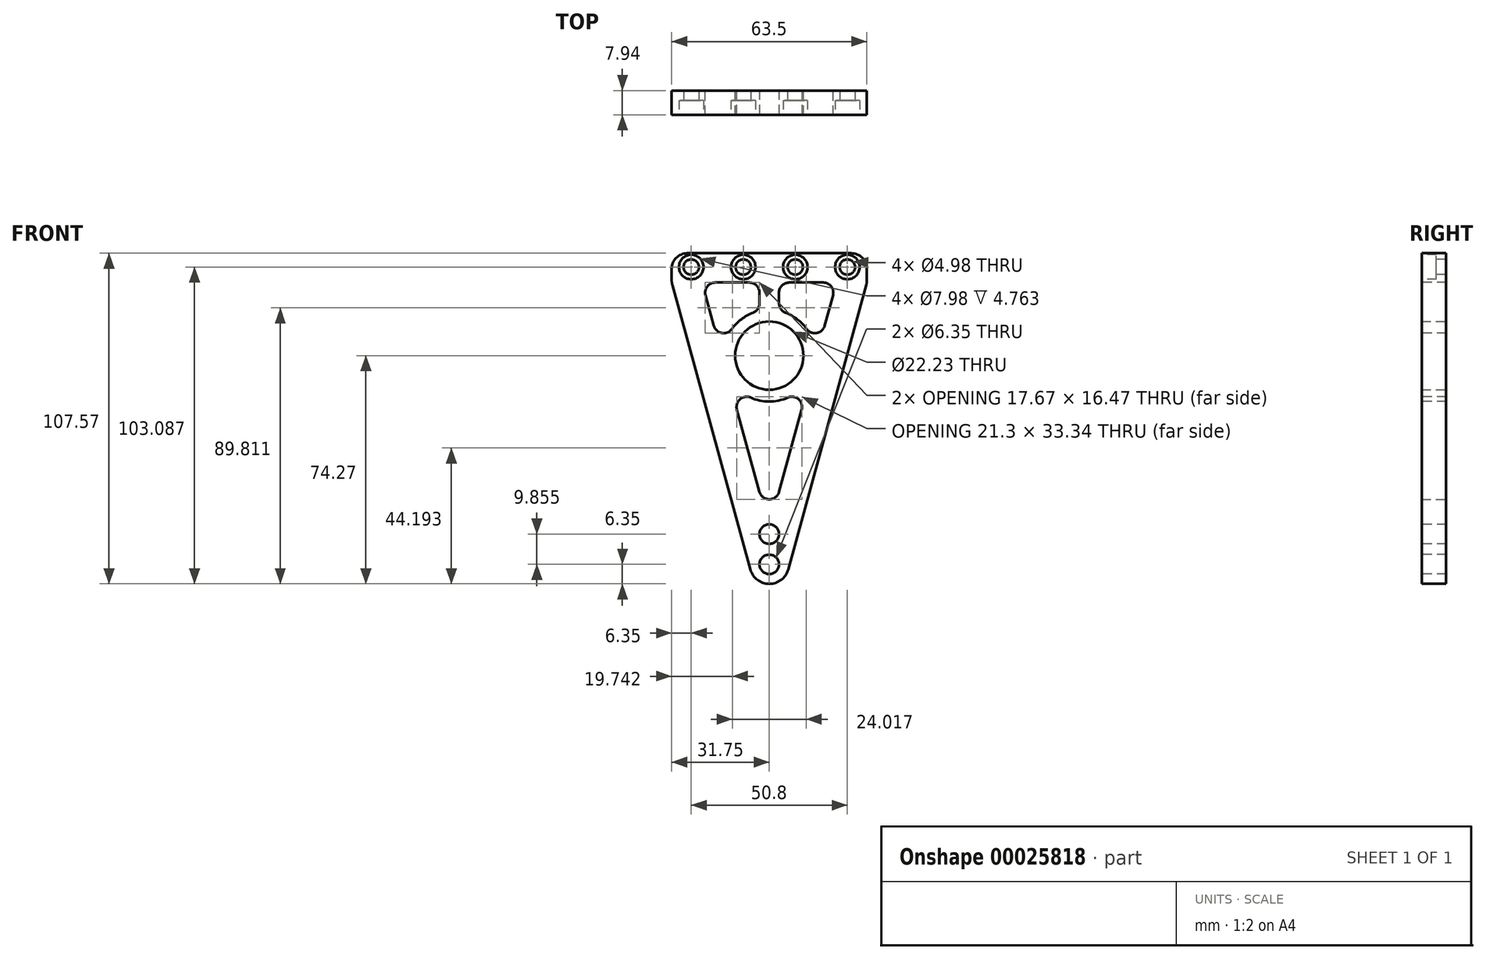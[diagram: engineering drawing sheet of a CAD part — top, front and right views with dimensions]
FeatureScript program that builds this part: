
annotation { "Feature Type Name" : "Feature", "Feature Type Description" : "" }
export const myFeature = defineFeature(function(context is Context, id is Id, definition is map)
    precondition{}
    {
        {
            var Q0;
            Q0=qCreatedBy(makeId("Front.planeOp"),FACE);
            var sketch = newSketch(context, id + "F0", { "sketchPlane" : qUnion([Q0])});
            skCircle(sketch, "E0", {"center": v(0, 0) * mm, "radius": 11.11 * mm});
            skLineSegment(sketch, "E1", {"start": v(0, 0) * mm, "end": v(0, 33.3) * mm, "construction": true});
            skLineSegment(sketch, "E2", {"start": v(0, 0) * mm, "end": v(25.23, 0) * mm, "construction": true});
            skLineSegment(sketch, "E3", {"start": v(-31.75, 33.3) * mm, "end": v(31.75, 33.3) * mm});
            skLineSegment(sketch, "E4", {"start": v(31.75, 33.3) * mm, "end": v(31.75, 23.77) * mm});
            skLineSegment(sketch, "E5", {"start": v(31.75, 23.77) * mm, "end": v(6.12, -69.6) * mm});
            skLineSegment(sketch, "E6", {"start": v(-6.12, -69.6) * mm, "end": v(-31.75, 23.77) * mm});
            skLineSegment(sketch, "E7", {"start": v(-31.75, 23.77) * mm, "end": v(-31.75, 33.3) * mm});
            skArc(sketch, "E8", {"start": v(-6.12, -69.6) * mm, "mid": v(0, -74.27) * mm, "end": v(6.12, -69.6) * mm});
            skSolve(sketch);
        }
        {
            var Q0;
            Q0=makeQuery(id+"F0.imprint","IMPRINT",FACE,{"disambiguationData":[TD([[makeQuery(id+"F0.imprint","IMPRINT",EDGE,{"derivedFrom":sQuery(id+"F0.wireOp",EDGE,"E0")}),-1.0]])]});
            extrude(context, id + "F1", {"entities" : qUnion([Q0]), "depth" : 6.35 * mm});
        }
        {
            var Q0;
            Q0=makeQuery(id+"F1.opExtrude","CAP_FACE",FACE,{"disambiguationData":[OSD([sQuery(id+"F0.wireOp",EDGE,"E0"),sQuery(id+"F0.wireOp",EDGE,"E3"),sQuery(id+"F0.wireOp",EDGE,"E4"),sQuery(id+"F0.wireOp",EDGE,"E5"),sQuery(id+"F0.wireOp",EDGE,"E6"),sQuery(id+"F0.wireOp",EDGE,"E7"),sQuery(id+"F0.wireOp",EDGE,"E8")])],"isStart":false});
            var sketch = newSketch(context, id + "F2", { "sketchPlane" : qUnion([Q0])});
            skLineSegment(sketch, "E9.0", {"start": v(21.87, 23.77) * mm, "end": v(3.17, 23.77) * mm});
            skLineSegment(sketch, "E9.2", {"start": v(0, -55.92) * mm, "end": v(13.77, -5.75) * mm});
            skLineSegment(sketch, "E9.3", {"start": v(-21.87, 23.77) * mm, "end": v(-14.78, -2.08) * mm});
            skArc(sketch, "E10", {"start": v(-13.77, -5.75) * mm, "mid": v(0, -14.92) * mm, "end": v(13.77, -5.75) * mm});
            skLineSegment(sketch, "E11.trimOffspring", {"start": v(-13.77, -5.75) * mm, "end": v(0, -55.92) * mm});
            skArc(sketch, "E12.trimOffspring", {"start": v(14.78, -2.08) * mm, "mid": v(12.25, 8.53) * mm, "end": v(3.18, 14.58) * mm});
            skLineSegment(sketch, "E13.trimOffspring", {"start": v(14.78, -2.08) * mm, "end": v(21.87, 23.77) * mm});
            skLineSegment(sketch, "E14", {"start": v(0, 0) * mm, "end": v(0, 33.3) * mm, "construction": true});
            skLineSegment(sketch, "E15.left", {"start": v(3.18, 14.58) * mm, "end": v(3.17, 23.77) * mm});
            skLineSegment(sketch, "E15.right", {"start": v(-3.18, 14.58) * mm, "end": v(-3.17, 23.77) * mm});
            skArc(sketch, "E16.trimOffspring", {"start": v(-3.18, 14.58) * mm, "mid": v(-12.25, 8.53) * mm, "end": v(-14.78, -2.08) * mm});
            skLineSegment(sketch, "E17.trimOffspring", {"start": v(-3.18, 23.77) * mm, "end": v(-21.87, 23.77) * mm});
            skSolve(sketch);
        }
        {
            var Q0;
            Q0=makeQuery(id+"F2.imprint","IMPRINT",FACE,{"disambiguationData":[TD([[makeQuery(id+"F2.imprint","IMPRINT",EDGE,{"derivedFrom":sQuery(id+"F2.wireOp",EDGE,"E9.0")}),1.0]])]});
            var Q1;
            Q1=makeQuery(id+"F2.imprint","IMPRINT",FACE,{"disambiguationData":[TD([[makeQuery(id+"F2.imprint","IMPRINT",EDGE,{"derivedFrom":sQuery(id+"F2.wireOp",EDGE,"E9.3")}),1.0]])]});
            var Q2;
            Q2=makeQuery(id+"F2.imprint","IMPRINT",FACE,{"disambiguationData":[TD([[makeQuery(id+"F2.imprint","IMPRINT",EDGE,{"derivedFrom":sQuery(id+"F2.wireOp",EDGE,"E9.2")}),1.0]])]});
            extrude(context, id + "F3", {"entities" : qUnion([Q0, Q1, Q2]), "operationType" : NewBodyOperationType.REMOVE, "endBound" : BoundingType.THROUGH_ALL, "oppositeDirection" : true, "depth" : 25.4 * mm});
        }
        {
            var Q0;
            Q0=makeQuery(id+"F3.boolean.opBoolean","COPY",EDGE,{"derivedFrom":makeQuery(id+"F3.opExtrude","SWEPT_EDGE",EDGE,{"disambiguationData":[OSD([sQuery(id+"F2.wireOp",EDGE,"E9.3"),sQuery(id+"F2.wireOp",EDGE,"E17.trimOffspring")])]})});
            var Q1;
            Q1=makeQuery(id+"F3.boolean.opBoolean","COPY",EDGE,{"derivedFrom":makeQuery(id+"F3.opExtrude","SWEPT_EDGE",EDGE,{"disambiguationData":[OSD([sQuery(id+"F2.wireOp",EDGE,"E15.right"),sQuery(id+"F2.wireOp",EDGE,"E16.trimOffspring")])]})});
            var Q2;
            Q2=makeQuery(id+"F3.boolean.opBoolean","COPY",EDGE,{"derivedFrom":makeQuery(id+"F3.opExtrude","SWEPT_EDGE",EDGE,{"disambiguationData":[OSD([sQuery(id+"F2.wireOp",EDGE,"E9.3"),sQuery(id+"F2.wireOp",EDGE,"E16.trimOffspring")])]})});
            var Q3;
            Q3=makeQuery(id+"F3.boolean.opBoolean","COPY",EDGE,{"derivedFrom":makeQuery(id+"F3.opExtrude","SWEPT_EDGE",EDGE,{"disambiguationData":[OSD([sQuery(id+"F2.wireOp",EDGE,"E9.0"),sQuery(id+"F2.wireOp",EDGE,"E13.trimOffspring")])]})});
            var Q4;
            Q4=makeQuery(id+"F3.boolean.opBoolean","COPY",EDGE,{"derivedFrom":makeQuery(id+"F3.opExtrude","SWEPT_EDGE",EDGE,{"disambiguationData":[OSD([sQuery(id+"F2.wireOp",EDGE,"E9.0"),sQuery(id+"F2.wireOp",EDGE,"E15.left")])]})});
            var Q5;
            Q5=makeQuery(id+"F3.boolean.opBoolean","COPY",EDGE,{"derivedFrom":makeQuery(id+"F3.opExtrude","SWEPT_EDGE",EDGE,{"disambiguationData":[OSD([sQuery(id+"F2.wireOp",EDGE,"E12.trimOffspring"),sQuery(id+"F2.wireOp",EDGE,"E13.trimOffspring")])]})});
            var Q6;
            Q6=makeQuery(id+"F3.boolean.opBoolean","COPY",EDGE,{"derivedFrom":makeQuery(id+"F3.opExtrude","SWEPT_EDGE",EDGE,{"disambiguationData":[OSD([sQuery(id+"F2.wireOp",EDGE,"E9.2"),sQuery(id+"F2.wireOp",EDGE,"E10")])]})});
            var Q7;
            Q7=makeQuery(id+"F3.boolean.opBoolean","COPY",EDGE,{"derivedFrom":makeQuery(id+"F3.opExtrude","SWEPT_EDGE",EDGE,{"disambiguationData":[OSD([sQuery(id+"F2.wireOp",EDGE,"E10"),sQuery(id+"F2.wireOp",EDGE,"E11.trimOffspring")])]})});
            var Q8;
            Q8=makeQuery(id+"F3.boolean.opBoolean","COPY",EDGE,{"derivedFrom":makeQuery(id+"F3.opExtrude","SWEPT_EDGE",EDGE,{"disambiguationData":[OSD([sQuery(id+"F2.wireOp",EDGE,"E9.2"),sQuery(id+"F2.wireOp",EDGE,"E11.trimOffspring")])]})});
            var Q9;
            Q9=makeQuery(id+"F3.boolean.opBoolean","COPY",EDGE,{"derivedFrom":makeQuery(id+"F3.opExtrude","SWEPT_EDGE",EDGE,{"disambiguationData":[OSD([sQuery(id+"F2.wireOp",EDGE,"E15.right"),sQuery(id+"F2.wireOp",EDGE,"E17.trimOffspring")])]})});
            var Q10;
            Q10=makeQuery(id+"F3.boolean.opBoolean","COPY",EDGE,{"derivedFrom":makeQuery(id+"F3.opExtrude","SWEPT_EDGE",EDGE,{"disambiguationData":[OSD([sQuery(id+"F2.wireOp",EDGE,"E12.trimOffspring"),sQuery(id+"F2.wireOp",EDGE,"E15.left")])]})});
            fillet(context, id + "F4", {"entities" : qUnion([Q0, Q1, Q2, Q3, Q4, Q5, Q6, Q7, Q8, Q9, Q10]), "radius" : 3.3 * mm, "tangentPropagation" : true, "allowEdgeOverflow" : false});
        }
        {
            var Q0;
            Q0=makeQuery(id+"F1.opExtrude","CAP_FACE",FACE,{"disambiguationData":[OSD([sQuery(id+"F0.wireOp",EDGE,"E0"),sQuery(id+"F0.wireOp",EDGE,"E3"),sQuery(id+"F0.wireOp",EDGE,"E4"),sQuery(id+"F0.wireOp",EDGE,"E5"),sQuery(id+"F0.wireOp",EDGE,"E6"),sQuery(id+"F0.wireOp",EDGE,"E7"),sQuery(id+"F0.wireOp",EDGE,"E8")])],"isStart":false});
            var sketch = newSketch(context, id + "F5", { "sketchPlane" : qUnion([Q0])});
            skCircle(sketch, "E18", {"center": v(0, -58.06) * mm, "radius": 3.18 * mm});
            skCircle(sketch, "E19", {"center": v(0, -67.92) * mm, "radius": 3.18 * mm});
            skLineSegment(sketch, "E20", {"start": v(-25.4, 28.82) * mm, "end": v(25.4, 28.82) * mm});
            skPoint(sketch, "E21", {"position": v(-8.46, 28.82) * mm});
            skPoint(sketch, "E22", {"position": v(8.46, 28.82) * mm});
            skLineSegment(sketch, "E23", {"start": v(0, 0) * mm, "end": v(0, 33.3) * mm, "construction": true});
            skSolve(sketch);
        }
        {
            var Q0;
            Q0=sQuery(id+"F5.wireOp",VERTEX,"E18.center");
            var Q1;
            Q1=sQuery(id+"F5.wireOp",VERTEX,"E19.center");
            var Q2;
            Q2=makeQuery(id+"F1.opExtrude","SWEPT_BODY",BODY,{"disambiguationData":[OSD([sQuery(id+"F0.wireOp",EDGE,"E0"),sQuery(id+"F0.wireOp",EDGE,"E3"),sQuery(id+"F0.wireOp",EDGE,"E4"),sQuery(id+"F0.wireOp",EDGE,"E5"),sQuery(id+"F0.wireOp",EDGE,"E6"),sQuery(id+"F0.wireOp",EDGE,"E7"),sQuery(id+"F0.wireOp",EDGE,"E8")])]});
            hole(context, id + "F6", {"style" : HoleStyle.SIMPLE, "holeDiameter" : 6.35 * mm, "endStyle" : HoleEndStyle.THROUGH, "locations" : qUnion([Q0, Q1]), "scope" : qUnion([Q2])});
        }
        {
            var Q0;
            Q0=sQuery(id+"F5.wireOp",VERTEX,"E20.start");
            var Q1;
            Q1=sQuery(id+"F5.wireOp",VERTEX,"E21");
            var Q2;
            Q2=sQuery(id+"F5.wireOp",VERTEX,"E22");
            var Q3;
            Q3=sQuery(id+"F5.wireOp",VERTEX,"E20.end");
            var Q4;
            Q4=makeQuery(id+"F1.opExtrude","SWEPT_BODY",BODY,{"disambiguationData":[OSD([sQuery(id+"F0.wireOp",EDGE,"E0"),sQuery(id+"F0.wireOp",EDGE,"E3"),sQuery(id+"F0.wireOp",EDGE,"E4"),sQuery(id+"F0.wireOp",EDGE,"E5"),sQuery(id+"F0.wireOp",EDGE,"E6"),sQuery(id+"F0.wireOp",EDGE,"E7"),sQuery(id+"F0.wireOp",EDGE,"E8")])]});
            hole(context, id + "F7", {"style" : HoleStyle.C_BORE, "holeDiameter" : 4.98 * mm, "cBoreDiameter" : 7.98 * mm, "cBoreDepth" : 3.17 * mm, "endStyle" : HoleEndStyle.THROUGH, "locations" : qUnion([Q0, Q1, Q2, Q3]), "scope" : qUnion([Q4])});
        }
        {
            var Q0;
            Q0=makeQuery(id+"F1.opExtrude","SWEPT_EDGE",EDGE,{"disambiguationData":[OSD([sQuery(id+"F0.wireOp",EDGE,"E3"),sQuery(id+"F0.wireOp",EDGE,"E4")])]});
            var Q1;
            Q1=makeQuery(id+"F1.opExtrude","SWEPT_EDGE",EDGE,{"disambiguationData":[OSD([sQuery(id+"F0.wireOp",EDGE,"E3"),sQuery(id+"F0.wireOp",EDGE,"E7")])]});
            var Q2;
            Q2=makeQuery(id+"F1.opExtrude","SWEPT_EDGE",EDGE,{"disambiguationData":[OSD([sQuery(id+"F0.wireOp",EDGE,"E6"),sQuery(id+"F0.wireOp",EDGE,"E7")])]});
            var Q3;
            Q3=makeQuery(id+"F1.opExtrude","SWEPT_EDGE",EDGE,{"disambiguationData":[OSD([sQuery(id+"F0.wireOp",EDGE,"E4"),sQuery(id+"F0.wireOp",EDGE,"E5")])]});
            fillet(context, id + "F8", {"entities" : qUnion([Q0, Q1, Q2, Q3]), "radius" : 5.08 * mm, "tangentPropagation" : true, "allowEdgeOverflow" : false});
        }
        {
            var Q0;
            Q0=makeQuery(id+"F1.opExtrude","CAP_FACE",FACE,{"disambiguationData":[OSD([sQuery(id+"F0.wireOp",EDGE,"E0"),sQuery(id+"F0.wireOp",EDGE,"E3"),sQuery(id+"F0.wireOp",EDGE,"E4"),sQuery(id+"F0.wireOp",EDGE,"E5"),sQuery(id+"F0.wireOp",EDGE,"E6"),sQuery(id+"F0.wireOp",EDGE,"E7"),sQuery(id+"F0.wireOp",EDGE,"E8")])],"isStart":false});
            extrude(context, id + "F9", {"entities" : qUnion([Q0]), "operationType" : NewBodyOperationType.ADD, "depth" : 1.59 * mm});
        }
    });
